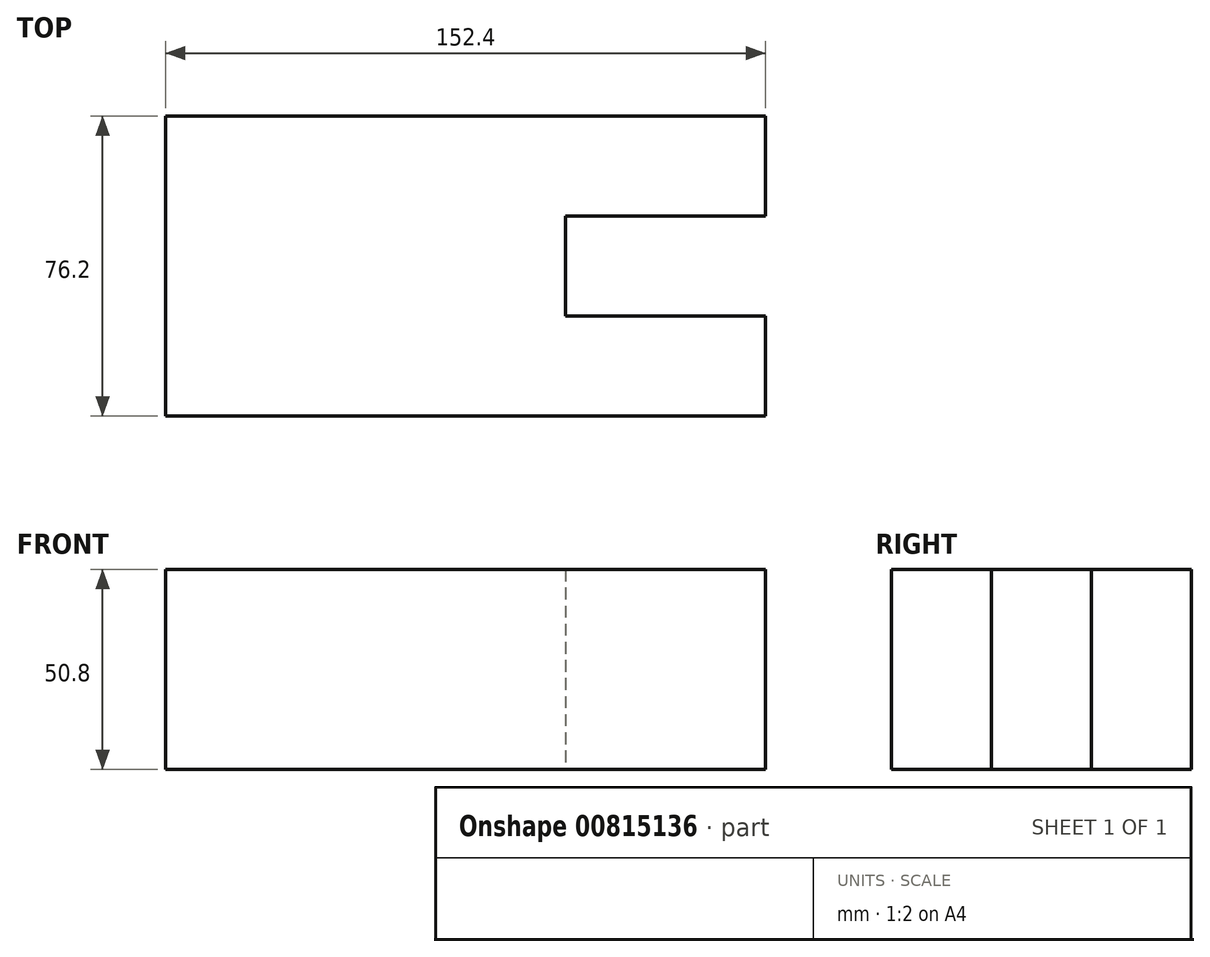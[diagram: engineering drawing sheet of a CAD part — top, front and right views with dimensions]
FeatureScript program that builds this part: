
annotation { "Feature Type Name" : "Feature", "Feature Type Description" : "" }
export const myFeature = defineFeature(function(context is Context, id is Id, definition is map)
    precondition{}
    {
        {
            var Q0;
            Q0=qCreatedBy(makeId("Top.planeOp"),FACE);
            var sketch = newSketch(context, id + "F0", { "sketchPlane" : qUnion([Q0])});
            skLineSegment(sketch, "E0", {"start": v(-64.69, 79.75) * mm, "end": v(-64.69, 3.55) * mm});
            skLineSegment(sketch, "E1", {"start": v(-64.69, 3.55) * mm, "end": v(87.71, 3.55) * mm});
            skLineSegment(sketch, "E2", {"start": v(87.71, 3.55) * mm, "end": v(87.71, 28.95) * mm});
            skLineSegment(sketch, "E3", {"start": v(87.71, 28.95) * mm, "end": v(36.91, 28.95) * mm});
            skLineSegment(sketch, "E4", {"start": v(36.91, 28.95) * mm, "end": v(36.91, 54.35) * mm});
            skLineSegment(sketch, "E5", {"start": v(36.91, 54.35) * mm, "end": v(87.71, 54.35) * mm});
            skLineSegment(sketch, "E6", {"start": v(87.71, 54.35) * mm, "end": v(87.71, 79.75) * mm});
            skLineSegment(sketch, "E7", {"start": v(87.71, 79.75) * mm, "end": v(-64.69, 79.75) * mm});
            skSolve(sketch);
        }
        {
            var Q0;
            Q0=makeQuery(id+"F0.imprint","IMPRINT",FACE,{"disambiguationData":[TD([[makeQuery(id+"F0.imprint","IMPRINT",EDGE,{"derivedFrom":sQuery(id+"F0.wireOp",EDGE,"E0")}),1.0]])]});
            extrude(context, id + "F1", {"entities" : qUnion([Q0]), "depth" : 50.8 * mm, "offsetDistance" : 25.4 * mm});
        }
    });
